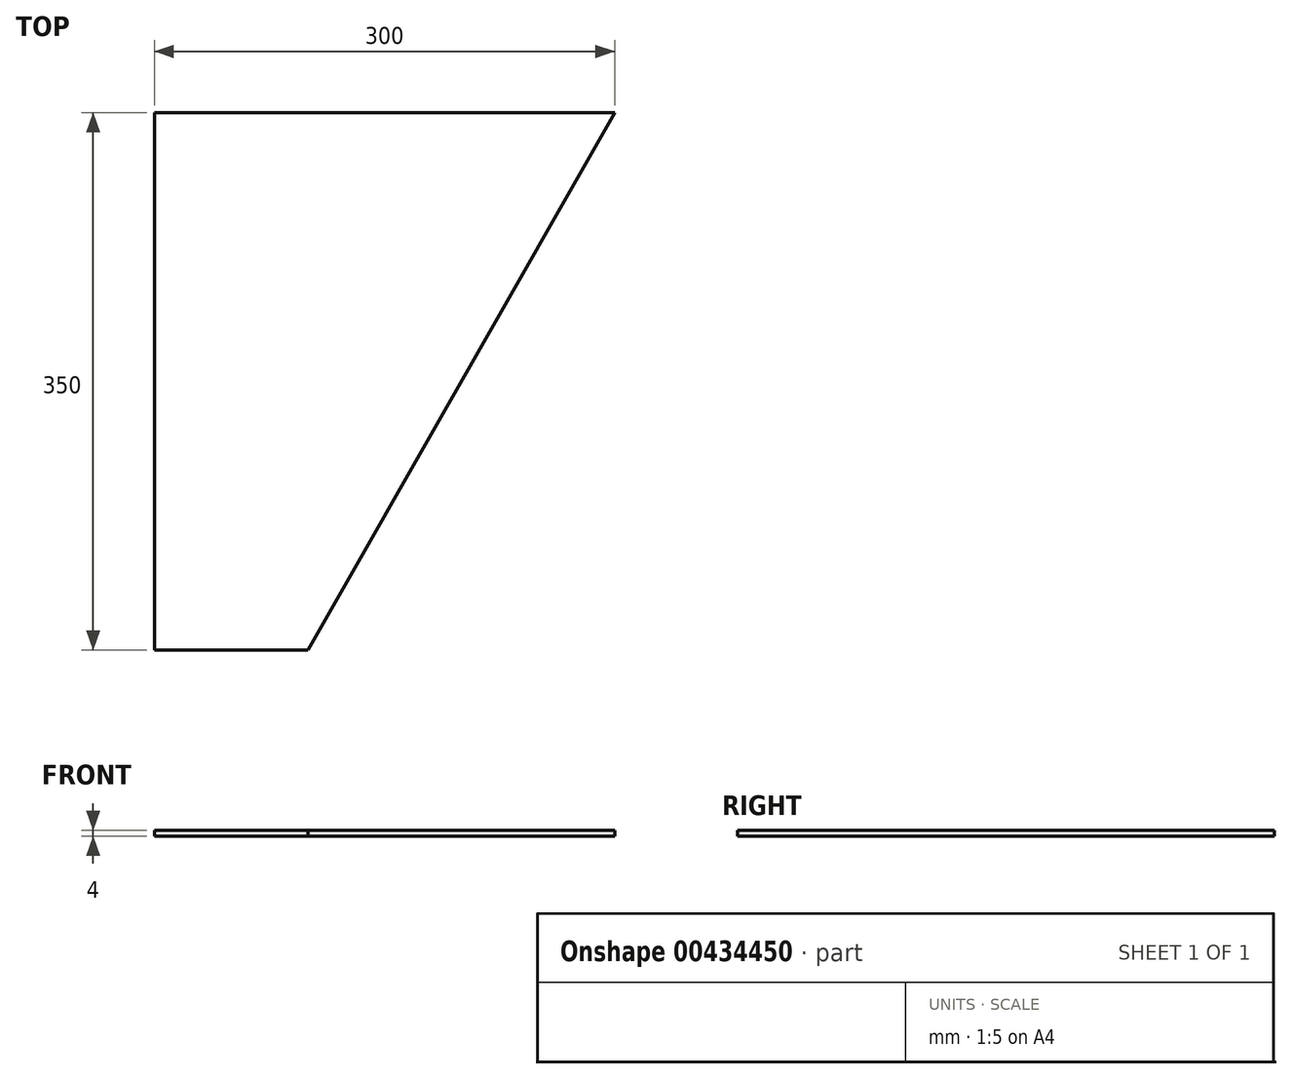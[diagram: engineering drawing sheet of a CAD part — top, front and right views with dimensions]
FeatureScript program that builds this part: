
annotation { "Feature Type Name" : "Feature", "Feature Type Description" : "" }
export const myFeature = defineFeature(function(context is Context, id is Id, definition is map)
    precondition{}
    {
        {
            var Q0;
            Q0=qCreatedBy(makeId("Top.planeOp"),FACE);
            var sketch = newSketch(context, id + "F0", { "sketchPlane" : qUnion([Q0])});
            skLineSegment(sketch, "E0", {"start": v(0, 0) * mm, "end": v(0, 700) * mm});
            skLineSegment(sketch, "E1", {"start": v(0, 700) * mm, "end": v(400, 700) * mm});
            skLineSegment(sketch, "E2", {"start": v(0, 0) * mm, "end": v(0, 0) * mm});
            skLineSegment(sketch, "E3", {"start": v(400, 700) * mm, "end": v(0, 0) * mm});
            skSolve(sketch);
        }
        {
            var Q0;
            Q0 = qSketchRegion(id + "F0", true);
            extrude(context, id + "F1", {"entities" : qUnion([Q0]), "depth" : 4 * mm, "offsetDistance" : 25 * mm});
        }
        {
            var Q0;
            Q0=makeQuery(id+"F1.opExtrude","CAP_FACE",FACE,{"disambiguationData":[OSD([sQuery(id+"F0.wireOp",EDGE,"E0"),sQuery(id+"F0.wireOp",EDGE,"E1"),sQuery(id+"F0.wireOp",EDGE,"E3")])],"isStart":false});
            var sketch = newSketch(context, id + "F2", { "sketchPlane" : qUnion([Q0])});
            skLineSegment(sketch, "E4", {"start": v(0, 250) * mm, "end": v(100, 250) * mm});
            skLineSegment(sketch, "E5", {"start": v(100, 250) * mm, "end": v(300, 600) * mm});
            skLineSegment(sketch, "E6", {"start": v(300, 600) * mm, "end": v(0, 600) * mm});
            skLineSegment(sketch, "E7", {"start": v(0, 600) * mm, "end": v(0, 700) * mm});
            skLineSegment(sketch, "E8", {"start": v(0, 700) * mm, "end": v(400, 700) * mm});
            skLineSegment(sketch, "E9", {"start": v(400, 700) * mm, "end": v(0, 0) * mm});
            skLineSegment(sketch, "E10", {"start": v(0, 0) * mm, "end": v(0, 250) * mm});
            skSolve(sketch);
        }
        {
            var Q0;
            Q0 = qSketchRegion(id + "F2", true);
            extrude(context, id + "F3", {"entities" : qUnion([Q0]), "operationType" : NewBodyOperationType.REMOVE, "endBound" : BoundingType.UP_TO_NEXT, "oppositeDirection" : true, "depth" : 25 * mm, "offsetDistance" : 25 * mm});
        }
    });
